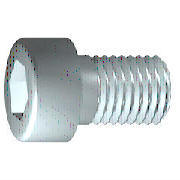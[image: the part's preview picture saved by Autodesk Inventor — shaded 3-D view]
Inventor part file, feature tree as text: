
AUTODESK INVENTOR PART (.ipt)
format: ipt  version: 2019 (Build 230136000, 136)  size: 198,144 bytes
history: native  units: mm (DEFAULTED — no unit token found)
features: sketch x2, extrude x1, plane x1, fillet x1
ambient origin geometry x7: Origin, YZ Plane, XY Plane, X Axis, Y Axis, Z Axis, Center Point
bodies: Solid1 (feature_tree), Body (feature_tree)
feature tree (5):
  extrude  "Slot"  Depth=5.0mm
  plane  "Work Plane1"
  fillet  "Fillet2"  Radius=5.0mm
  sketch  "Sketch1"  dims[d1=16.0mm d2=0.49086mm d3=5.0mm]
  sketch  "Sketch2"  dims[d4=2.5mm d5=60.0deg d6=5.0mm d7=5.0mm d8=4.618802mm d9=8.5mm d10=90.0deg d11=10.0mm d12=0.0mm d13=16.0mm d14=0.0mm d15=0.49076mm d16=0.49076mm d17=0.5mm d19=0.0mm d26=30.0mm d27=45.0deg d28=0.0mm d29=0.0mm d30=0.1mm]
